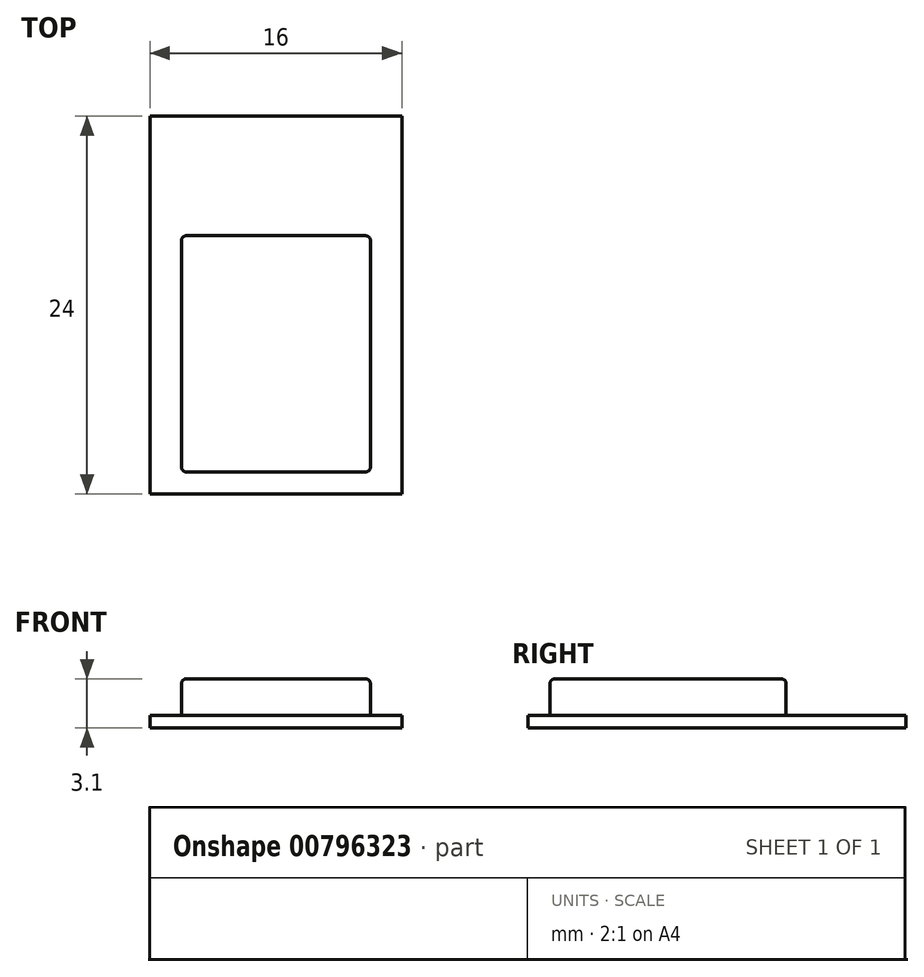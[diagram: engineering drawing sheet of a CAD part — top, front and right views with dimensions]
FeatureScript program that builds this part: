
annotation { "Feature Type Name" : "Feature", "Feature Type Description" : "" }
export const myFeature = defineFeature(function(context is Context, id is Id, definition is map)
    precondition{}
    {
        {
            var Q0;
            Q0=qCreatedBy(makeId("Top.planeOp"),FACE);
            var sketch = newSketch(context, id + "F0", { "sketchPlane" : qUnion([Q0])});
            skLineSegment(sketch, "E0.bottom", {"start": v(8, 12) * mm, "end": v(-8, 12) * mm});
            skLineSegment(sketch, "E0.top", {"start": v(8, -12) * mm, "end": v(-8, -12) * mm});
            skLineSegment(sketch, "E0.left", {"start": v(8, 12) * mm, "end": v(8, -12) * mm});
            skLineSegment(sketch, "E0.right", {"start": v(-8, 12) * mm, "end": v(-8, -12) * mm});
            skPoint(sketch, "E0.middle", {"position": v(0, 0) * mm});
            skSolve(sketch);
        }
        {
            var Q0;
            Q0 = qSketchRegion(id + "F0", true);
            extrude(context, id + "F1", {"entities" : qUnion([Q0]), "depth" : .8 * mm, "offsetDistance" : 25 * mm});
        }
        {
            var Q0;
            Q0=makeQuery(id+"F1.opExtrude","CAP_FACE",FACE,{"disambiguationData":[OSD([sQuery(id+"F0.wireOp",EDGE,"E0.bottom"),sQuery(id+"F0.wireOp",EDGE,"E0.top"),sQuery(id+"F0.wireOp",EDGE,"E0.left"),sQuery(id+"F0.wireOp",EDGE,"E0.right")])],"isStart":false});
            var sketch = newSketch(context, id + "F2", { "sketchPlane" : qUnion([Q0])});
            skLineSegment(sketch, "E1", {"start": v(0, -0.69) * mm, "end": v(0, -13.66) * mm, "construction": true});
            skLineSegment(sketch, "E2.bottom", {"start": v(6, 4.4) * mm, "end": v(-6, 4.4) * mm});
            skLineSegment(sketch, "E2.top", {"start": v(6, -10.6) * mm, "end": v(-6, -10.6) * mm});
            skLineSegment(sketch, "E2.left", {"start": v(6, 4.4) * mm, "end": v(6, -10.6) * mm});
            skLineSegment(sketch, "E2.right", {"start": v(-6, 4.4) * mm, "end": v(-6, -10.6) * mm});
            skPoint(sketch, "E2.middle", {"position": v(0, -3.1) * mm});
            skSolve(sketch);
        }
        {
            var Q0;
            Q0 = qSketchRegion(id + "F2", true);
            extrude(context, id + "F3", {"entities" : qUnion([Q0]), "depth" : 2.3 * mm, "offsetDistance" : 25 * mm});
        }
        {
            var Q0;
            Q0=makeQuery(id+"F3.opExtrude","CAP_FACE",FACE,{"disambiguationData":[OSD([sQuery(id+"F2.wireOp",EDGE,"E2.bottom"),sQuery(id+"F2.wireOp",EDGE,"E2.top"),sQuery(id+"F2.wireOp",EDGE,"E2.left"),sQuery(id+"F2.wireOp",EDGE,"E2.right")])],"isStart":false});
            var Q1;
            Q1=makeQuery(id+"F3.opExtrude","SWEPT_EDGE",EDGE,{"disambiguationData":[OSD([sQuery(id+"F2.wireOp",EDGE,"E2.bottom"),sQuery(id+"F2.wireOp",EDGE,"E2.right")])]});
            var Q2;
            Q2=makeQuery(id+"F3.opExtrude","SWEPT_EDGE",EDGE,{"disambiguationData":[OSD([sQuery(id+"F2.wireOp",EDGE,"E2.bottom"),sQuery(id+"F2.wireOp",EDGE,"E2.left")])]});
            var Q3;
            Q3=makeQuery(id+"F3.opExtrude","SWEPT_EDGE",EDGE,{"disambiguationData":[OSD([sQuery(id+"F2.wireOp",EDGE,"E2.top"),sQuery(id+"F2.wireOp",EDGE,"E2.right")])]});
            var Q4;
            Q4=makeQuery(id+"F3.opExtrude","SWEPT_EDGE",EDGE,{"disambiguationData":[OSD([sQuery(id+"F2.wireOp",EDGE,"E2.top"),sQuery(id+"F2.wireOp",EDGE,"E2.left")])]});
            fillet(context, id + "F4", {"entities" : qUnion([Q0, Q1, Q2, Q3, Q4]), "radius" : .3 * mm, "tangentPropagation" : true, "allowEdgeOverflow" : false});
        }
    });
